# Revit family: CSL
name_source: partatom
category: Lighting Fixtures
revit_build: Autodesk Revit 2013 (Build: 20120221_2030(x64)
units: mm (PartAtom-declared; Revit-internal decimal feet)

## types (4) — shared parameters
Backbox = Hubbell - White
Color Filter = 16777215
Default Elevation = 4' - 0"
Description = LED Striplight
Dimming = 0-10V
Dimming Lamp Color Temperature Shift = <None>
Emit Shape Visible in Rendering = No
Emit from Rectangle Width = 0' - 2 1/2"
Glass = Hubbell - White Glass
Lamp = LED Lamp
Load Classification = Lighting
Manufacturer = Columbia Lighting
Manufacturer Fax = 866-898-1065
Model = CSL4
Mounting = Surface mount on wall or ceiling
Photometric Web File = generic.ies
Power Factor = 1
Product Documentation Link = http://cdn.columbialighting.com
Product Page URL = http://www.columbialighting.com
Tilt Angle = -90.00°
URL = http://www.columbialighting.com
Voltage = 120 V
Warranty = Five Year Warranty
Wattage Comments = 40.2W-80.5W

## per-type parameters (varying)
| type | Apparent Load | Emit from Rectangle Length | Row Length | Watts |
| CSL4-4035 | 40 VA | 3' - 11 1/2" | 4' - 0" | 40 W |
| CSL4-4040 | 40 VA | 3' - 11 1/2" | 4' - 0" | 40 W |
| CSL8-8035 | 81 VA | 7' - 11 1/2" | 8' - 0" | 81 W |
| CSL8-8040 | 81 VA | 7' - 11 1/2" | 8' - 0" | 81 W |

## geometry (parser evidence)
native form markers: Sweep x4
no freeform markers — native parametric forms only
